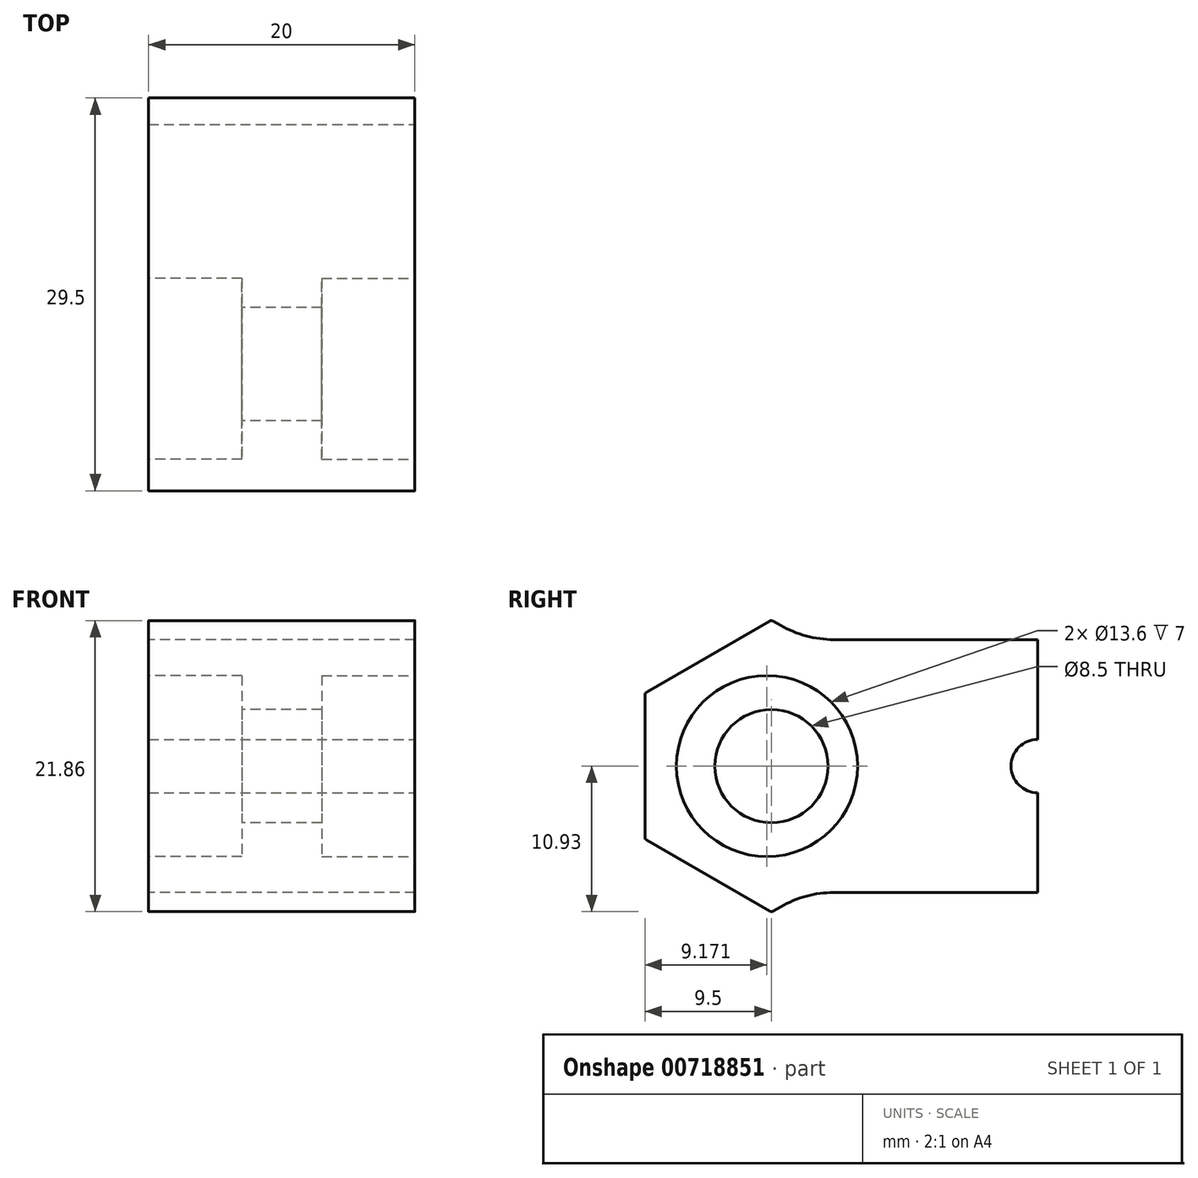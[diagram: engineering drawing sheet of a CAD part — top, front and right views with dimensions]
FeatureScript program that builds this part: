
annotation { "Feature Type Name" : "Feature", "Feature Type Description" : "" }
export const myFeature = defineFeature(function(context is Context, id is Id, definition is map)
    precondition{}
    {
        {
            var Q0;
            Q0=qCreatedBy(makeId("Right.planeOp"),FACE);
            var sketch = newSketch(context, id + "F0", { "sketchPlane" : qUnion([Q0])});
            skCircle(sketch, "E0.cCircle", {"center": v(0, 0) * mm, "radius": 9.5 * mm, "construction": true});
            skLineSegment(sketch, "E0.0", {"start": v(0, 10.97) * mm, "end": v(9.5, 5.48) * mm});
            skLineSegment(sketch, "E0.1", {"start": v(9.5, 5.48) * mm, "end": v(9.5, -5.48) * mm});
            skLineSegment(sketch, "E0.2", {"start": v(9.5, -5.48) * mm, "end": v(0, -10.97) * mm});
            skLineSegment(sketch, "E0.3", {"start": v(0, -10.97) * mm, "end": v(-9.5, -5.48) * mm});
            skLineSegment(sketch, "E0.4", {"start": v(-9.5, -5.48) * mm, "end": v(-9.5, 5.48) * mm});
            skLineSegment(sketch, "E0.5", {"start": v(-9.5, 5.48) * mm, "end": v(0, 10.97) * mm});
            skPoint(sketch, "E0.0.midPoint", {"position": v(4.75, 8.23) * mm});
            skLineSegment(sketch, "E1", {"start": v(0, 9.5) * mm, "end": v(20, 9.5) * mm});
            skLineSegment(sketch, "E2", {"start": v(0, 0) * mm, "end": v(20, 0) * mm});
            skLineSegment(sketch, "E3", {"start": v(2.55, -9.5) * mm, "end": v(20, -9.5) * mm});
            skLineSegment(sketch, "E4", {"start": v(20, 9.5) * mm, "end": v(20, -9.5) * mm});
            skSolve(sketch);
        }
        {
            var Q0;
            Q0=makeQuery(id+"F0.imprint","IMPRINT",FACE,{"disambiguationData":[TD([[makeQuery(id+"F0.imprint","IMPRINT",EDGE,{"derivedFrom":sQuery(id+"F0.wireOp",EDGE,"E0.0")}),-1.0]])]});
            var Q1;
            {var subQ9=sQuery(id+"F0.wireOp",EDGE,"RUkPWQqG-Jaeu-44Lu-u88V-SPSDFBEA0rpE");Q1=makeQuery(id+"F0.imprint","IMPRINT",FACE,{"disambiguationData":[TD([[makeQuery(id+"F0.imprint","IMPRINT",EDGE,{"derivedFrom":subQ9}),1.0]])]});}
            var Q2;
            {var subQ3=sQuery(id+"F0.wireOp",EDGE,"E0.1");var subQ7=sQuery(id+"F0.wireOp",EDGE,"E0.0");var subQ9=makeQuery(id+"F0.imprint","INTERSECT",VERTEX,{"derivedFrom":[subQ7,subQ3]});Q2=makeQuery(id+"F0.imprint","IMPRINT",FACE,{"disambiguationData":[TD([[makeQuery(id+"F0.imprint","IMPRINT",EDGE,{"disambiguationData":[TD([[subQ9,1.0]])],"derivedFrom":subQ7}),1.0]])]});}
            var Q3;
            {var subQ0=sQuery(id+"F0.wireOp",EDGE,"E3");Q3=makeQuery(id+"F0.imprint","IMPRINT",FACE,{"disambiguationData":[TD([[makeQuery(id+"F0.imprint","IMPRINT",EDGE,{"derivedFrom":subQ0}),1.0]])]});}
            extrude(context, id + "F1", {"entities" : qUnion([Q0, Q1, Q2, Q3]), "depth" : 20 * mm, "offsetDistance" : 25 * mm});
        }
        {
            var Q0;
            Q0=makeQuery(id+"F1.opExtrude","CAP_FACE",FACE,{"disambiguationData":[OSD([sQuery(id+"F0.wireOp",EDGE,"E0.0"),sQuery(id+"F0.wireOp",EDGE,"E0.1"),sQuery(id+"F0.wireOp",EDGE,"E0.2"),sQuery(id+"F0.wireOp",EDGE,"E0.3"),sQuery(id+"F0.wireOp",EDGE,"E0.4"),sQuery(id+"F0.wireOp",EDGE,"E0.5")])],"isStart":false});
            var Q1;
            Q1=makeQuery(id+"F1.opExtrude","CAP_FACE",FACE,{"disambiguationData":[OSD([sQuery(id+"F0.wireOp",EDGE,"E0.0"),sQuery(id+"F0.wireOp",EDGE,"E0.1"),sQuery(id+"F0.wireOp",EDGE,"E0.2"),sQuery(id+"F0.wireOp",EDGE,"E0.3"),sQuery(id+"F0.wireOp",EDGE,"E0.4"),sQuery(id+"F0.wireOp",EDGE,"E0.5")])],"isStart":true});
            cPlane(context, id + "F2", {"entities" : qUnion([Q0, Q1]), "cplaneType" : CPlaneType.MID_PLANE, "offset" : 25 * mm, "width" : 150 * mm, "height" : 150 * mm});
        }
        {
            var Q0;
            Q0=makeQuery(id+"F1.opExtrude","CAP_FACE",FACE,{"disambiguationData":[OSD([sQuery(id+"F0.wireOp",EDGE,"E0.0"),sQuery(id+"F0.wireOp",EDGE,"E0.1"),sQuery(id+"F0.wireOp",EDGE,"E0.2"),sQuery(id+"F0.wireOp",EDGE,"E0.3"),sQuery(id+"F0.wireOp",EDGE,"E0.4"),sQuery(id+"F0.wireOp",EDGE,"E0.5")])],"isStart":true});
            var sketch = newSketch(context, id + "F3", { "sketchPlane" : qUnion([Q0])});
            skCircle(sketch, "E5", {"center": v(0, 0) * mm, "radius": 4.3 * mm});
            skSolve(sketch);
        }
        {
            var Q0;
            Q0=makeQuery(id+"F3.imprint","IMPRINT",FACE,{"disambiguationData":[TD([[makeQuery(id+"F3.imprint","IMPRINT",EDGE,{"derivedFrom":sQuery(id+"F3.wireOp",EDGE,"E5")}),-1.0]])]});
            var sketch = newSketch(context, id + "F4", { "sketchPlane" : qUnion([Q0])});
            skCircle(sketch, "E6", {"center": v(0, 0) * mm, "radius": 4.25 * mm});
            skSolve(sketch);
        }
        {
            var Q0;
            Q0=makeQuery(id+"F4.imprint","IMPRINT",FACE,{"disambiguationData":[TD([[makeQuery(id+"F4.imprint","IMPRINT",EDGE,{"derivedFrom":sQuery(id+"F4.wireOp",EDGE,"E6")}),1.0]])]});
            extrude(context, id + "F5", {"entities" : qUnion([Q0]), "operationType" : NewBodyOperationType.REMOVE, "endBound" : BoundingType.THROUGH_ALL, "oppositeDirection" : true, "depth" : 25 * mm, "offsetDistance" : 25 * mm});
        }
        {
            var Q0;
            Q0=makeQuery(id+"F1.opExtrude","CAP_FACE",FACE,{"disambiguationData":[OSD([sQuery(id+"F0.wireOp",EDGE,"E0.0"),sQuery(id+"F0.wireOp",EDGE,"E0.1"),sQuery(id+"F0.wireOp",EDGE,"E0.2"),sQuery(id+"F0.wireOp",EDGE,"E0.3"),sQuery(id+"F0.wireOp",EDGE,"E0.4"),sQuery(id+"F0.wireOp",EDGE,"E0.5")])],"isStart":true});
            var sketch = newSketch(context, id + "F6", { "sketchPlane" : qUnion([Q0])});
            skCircle(sketch, "E7", {"center": v(0.33, 0) * mm, "radius": 6.8 * mm});
            skSolve(sketch);
        }
        {
            var Q0;
            Q0=makeQuery(id+"F6.imprint","IMPRINT",FACE,{"disambiguationData":[TD([[makeQuery(id+"F6.imprint","IMPRINT",EDGE,{"derivedFrom":sQuery(id+"F6.wireOp",EDGE,"E7")}),1.0]])]});
            var Q1;
            Q1=makeQuery(id+"F6.imprint","IMPRINT",FACE,{"disambiguationData":[TD([[makeQuery(id+"F6.imprint","IMPRINT",EDGE,{"derivedFrom":makeQuery(id+"F5.boolean.opBoolean","COPY",EDGE,{"derivedFrom":makeQuery(id+"F5.opExtrude","CAP_EDGE",EDGE,{"disambiguationData":[OSD([sQuery(id+"F4.wireOp",EDGE,"E6")])],"isStart":true})})}),1.0]])]});
            extrude(context, id + "F7", {"entities" : qUnion([Q0, Q1]), "oppositeDirection" : true, "depth" : 7 * mm, "offsetDistance" : 25 * mm});
        }
        {
            var Q0;
            Q0=makeQuery(id+"F7.opExtrude","SWEPT_BODY",BODY,{"disambiguationData":[OSD([sQuery(id+"F6.wireOp",EDGE,"E7")])]});
            var Q1;
            Q1=qCreatedBy(id+"F2.planeOp",FACE);
            mirror(context, id + "F8", {"entities" : qUnion([Q0]), "mirrorPlane" : qUnion([Q1])});
        }
        {
            var Q0;
            Q0=makeQuery(id+"F7.opExtrude","SWEPT_BODY",BODY,{"disambiguationData":[OSD([sQuery(id+"F6.wireOp",EDGE,"E7")])]});
            var Q1;
            Q1=makeQuery(id+"F8.opPattern","COPY",BODY,{"derivedFrom":makeQuery(id+"F7.opExtrude","SWEPT_BODY",BODY,{"disambiguationData":[OSD([sQuery(id+"F6.wireOp",EDGE,"E7")])]}),"instanceName":"1"});
            var Q2;
            Q2=makeQuery(id+"F1.opExtrude","SWEPT_BODY",BODY,{"disambiguationData":[OSD([sQuery(id+"F0.wireOp",EDGE,"E0.0"),sQuery(id+"F0.wireOp",EDGE,"E0.1"),sQuery(id+"F0.wireOp",EDGE,"E0.2"),sQuery(id+"F0.wireOp",EDGE,"E0.3"),sQuery(id+"F0.wireOp",EDGE,"E0.4"),sQuery(id+"F0.wireOp",EDGE,"E0.5")])]});
            booleanBodies(context, id + "F9", {"operationType" : BooleanOperationType.SUBTRACTION, "tools" : qUnion([Q0, Q1]), "targets" : qUnion([Q2])});
        }
        {
            var Q0;
            Q0=makeQuery(id+"F1.opExtrude","SWEPT_EDGE",EDGE,{"disambiguationData":[OSD([sQuery(id+"F0.wireOp",EDGE,"E0.2"),sQuery(id+"F0.wireOp",EDGE,"E3")])]});
            var Q1;
            Q1=makeQuery(id+"F1.opExtrude","SWEPT_EDGE",EDGE,{"disambiguationData":[OSD([sQuery(id+"F0.wireOp",EDGE,"E0.0"),sQuery(id+"F0.wireOp",EDGE,"E1")])]});
            fillet(context, id + "F10", {"entities" : qUnion([Q0, Q1]), "radius" : 8 * mm, "tangentPropagation" : true, "allowEdgeOverflow" : false});
        }
        {
            var Q0;
            Q0=makeQuery(id+"F1.opExtrude","CAP_FACE",FACE,{"disambiguationData":[OSD([sQuery(id+"F0.wireOp",EDGE,"E0.0"),sQuery(id+"F0.wireOp",EDGE,"E0.2"),sQuery(id+"F0.wireOp",EDGE,"E0.3"),sQuery(id+"F0.wireOp",EDGE,"E0.4"),sQuery(id+"F0.wireOp",EDGE,"E0.5"),sQuery(id+"F0.wireOp",EDGE,"RUkPWQqG-Jaeu-44Lu-u88V-SPSDFBEA0rpE"),sQuery(id+"F0.wireOp",EDGE,"E1"),sQuery(id+"F0.wireOp",EDGE,"E3")])],"isStart":false});
            var sketch = newSketch(context, id + "F11", { "sketchPlane" : qUnion([Q0])});
            skCircle(sketch, "E8", {"center": v(20, 0) * mm, "radius": 2 * mm});
            skLineSegment(sketch, "E9", {"start": v(20, 0) * mm, "end": v(0, 0) * mm});
            skSolve(sketch);
        }
        {
            var Q0;
            Q0=makeQuery(id+"F11.imprint","IMPRINT",FACE,{"disambiguationData":[TD([[makeQuery(id+"F11.imprint","IMPRINT",EDGE,{"derivedFrom":sQuery(id+"F11.wireOp",EDGE,"E8")}),1.0]])]});
            extrude(context, id + "F12", {"entities" : qUnion([Q0]), "operationType" : NewBodyOperationType.REMOVE, "endBound" : BoundingType.THROUGH_ALL, "oppositeDirection" : true, "depth" : 25 * mm, "offsetDistance" : 25 * mm});
        }
        {
            var Q0;
            Q0=makeQuery(id+"F1.opExtrude","SWEPT_EDGE",EDGE,{"disambiguationData":[OSD([sQuery(id+"F0.wireOp",EDGE,"E0.3"),sQuery(id+"F0.wireOp",EDGE,"E0.4")])]});
            var Q1;
            Q1=makeQuery(id+"F1.opExtrude","SWEPT_EDGE",EDGE,{"disambiguationData":[OSD([sQuery(id+"F0.wireOp",EDGE,"E0.4"),sQuery(id+"F0.wireOp",EDGE,"E0.5")])]});
            var Q2;
            Q2=makeQuery(id+"F1.opExtrude","SWEPT_EDGE",EDGE,{"disambiguationData":[OSD([sQuery(id+"F0.wireOp",EDGE,"E0.0"),sQuery(id+"F0.wireOp",EDGE,"E0.5")])]});
            var Q3;
            Q3=makeQuery(id+"F1.opExtrude","SWEPT_EDGE",EDGE,{"disambiguationData":[OSD([sQuery(id+"F0.wireOp",EDGE,"E0.2"),sQuery(id+"F0.wireOp",EDGE,"E0.3")])]});
            fillet(context, id + "F13", {"entities" : qUnion([Q0, Q1, Q2, Q3]), "radius" : 0.25 * mm, "tangentPropagation" : true, "allowEdgeOverflow" : false});
        }
    });
